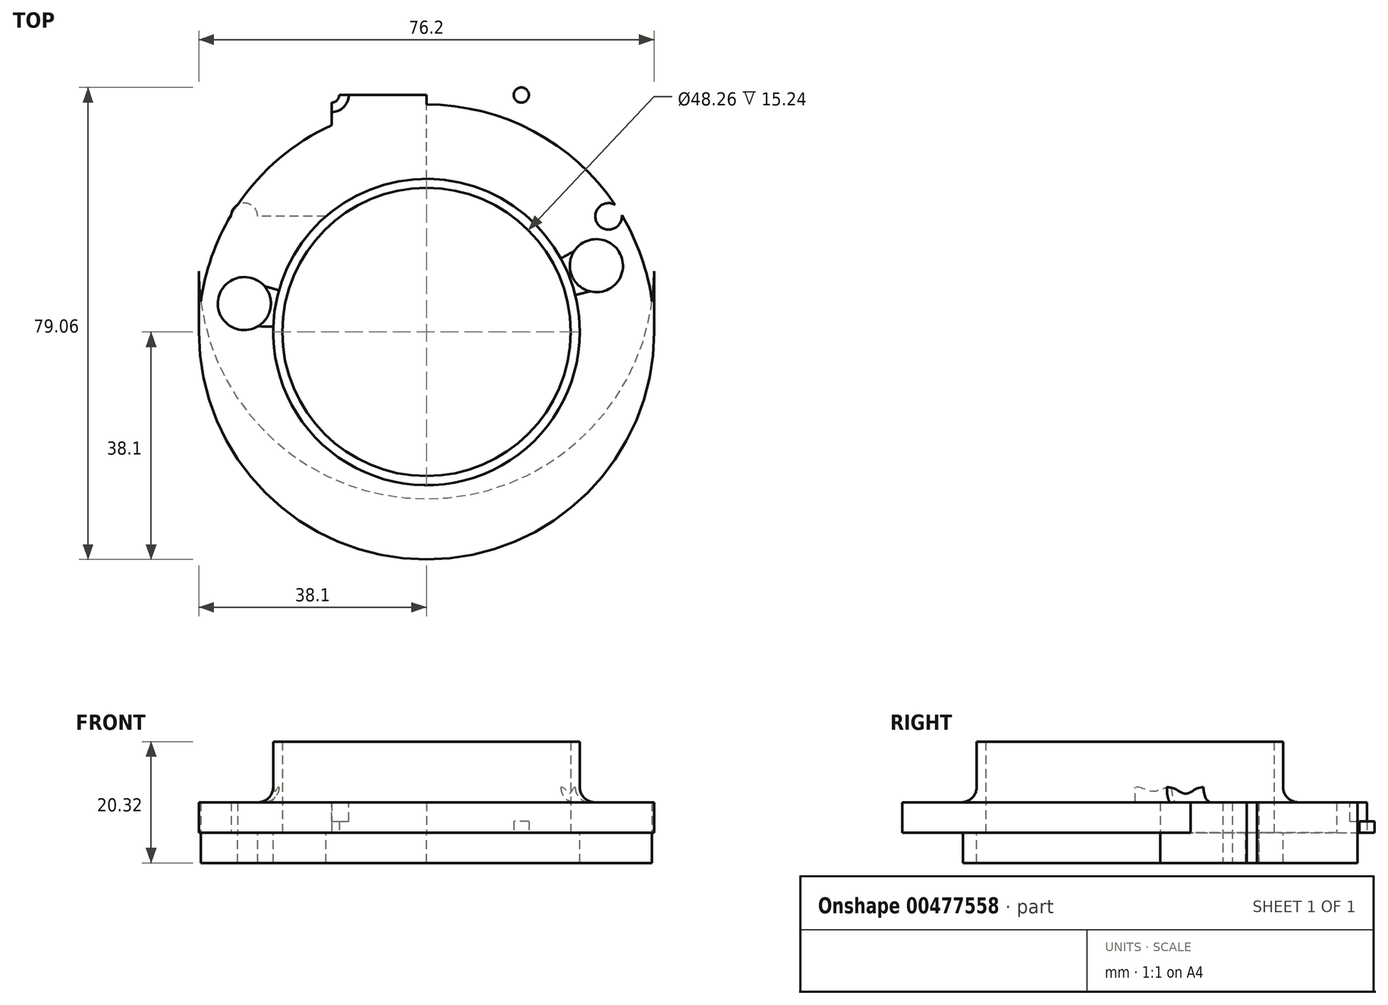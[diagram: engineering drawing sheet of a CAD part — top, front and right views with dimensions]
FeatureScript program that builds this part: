
annotation { "Feature Type Name" : "Feature", "Feature Type Description" : "" }
export const myFeature = defineFeature(function(context is Context, id is Id, definition is map)
    precondition{}
    {
        {
            var Q0;
            Q0=qCreatedBy(makeId("Top.planeOp"),FACE);
            var sketch = newSketch(context, id + "F0", { "sketchPlane" : qUnion([Q0])});
            skLineSegment(sketch, "E0", {"start": v(-15.88, 39.69) * mm, "end": v(15.88, 39.69) * mm});
            skLineSegment(sketch, "E1", {"start": v(0, 0) * mm, "end": v(0, 39.69) * mm});
            skCircle(sketch, "E2", {"center": v(-15.88, 39.69) * mm, "radius": 1.27 * mm});
            skLineSegment(sketch, "E3", {"start": v(-15.88, 19.37) * mm, "end": v(-15.88, 39.69) * mm});
            skCircle(sketch, "E4.MirrorC", {"center": v(15.88, 39.69) * mm, "radius": 1.27 * mm});
            skLineSegment(sketch, "E5", {"start": v(-15.88, 19.37) * mm, "end": v(-30.48, 19.37) * mm});
            skCircle(sketch, "E6", {"center": v(-30.48, 19.37) * mm, "radius": 2.22 * mm});
            skCircle(sketch, "E7.MirrorC", {"center": v(30.48, 19.37) * mm, "radius": 2.22 * mm});
            skCircle(sketch, "E8", {"center": v(0, 0) * mm, "radius": 24.13 * mm});
            skCircle(sketch, "E9", {"center": v(28.45, 11.11) * mm, "radius": 4.45 * mm});
            skCircle(sketch, "E10", {"center": v(-30.48, 4.76) * mm, "radius": 4.45 * mm});
            skCircle(sketch, "E11", {"center": v(0, 0) * mm, "radius": 25.65 * mm});
            skCircle(sketch, "E12", {"center": v(0, 0) * mm, "radius": 38.1 * mm});
            skCircle(sketch, "E13", {"center": v(0, 10.16) * mm, "radius": 38.1 * mm});
            skLineSegment(sketch, "E14", {"start": v(-38.1, 10.16) * mm, "end": v(-38.1, 0) * mm});
            skLineSegment(sketch, "E15", {"start": v(38.1, 10.16) * mm, "end": v(38.1, 0) * mm});
            skSolve(sketch);
        }
        {
            var Q0;
            Q0=makeQuery(id+"F0.imprint","IMPRINT",FACE,{"disambiguationData":[TD([[makeQuery(id+"F0.imprint","IMPRINT",EDGE,{"derivedFrom":sQuery(id+"F0.wireOp",EDGE,"E4.MirrorC")}),1.0]])]});
            var Q1;
            Q1=makeQuery(id+"F0.imprint","IMPRINT",FACE,{"disambiguationData":[TD([[makeQuery(id+"F0.imprint","IMPRINT",EDGE,{"derivedFrom":sQuery(id+"F0.wireOp",EDGE,"E7.MirrorC")}),-1.0]])]});
            var Q2;
            {var subQ1=sQuery(id+"F0.wireOp",EDGE,"E0");var subQ7=sQuery(id+"F0.wireOp",EDGE,"E1");var subQ8=makeQuery(id+"F0.imprint","INTERSECT",VERTEX,{"derivedFrom":[subQ1,subQ7]});Q2=makeQuery(id+"F0.imprint","IMPRINT",FACE,{"disambiguationData":[TD([[makeQuery(id+"F0.imprint","IMPRINT",EDGE,{"disambiguationData":[TD([[subQ8,1.0]])],"derivedFrom":subQ1}),-1.0]])]});}
            var Q3;
            {var subQ0=sQuery(id+"F0.wireOp",EDGE,"E11");var subQ1=sQuery(id+"F0.wireOp",EDGE,"E1");var subQ2=makeQuery(id+"F0.imprint","INTERSECT",VERTEX,{"derivedFrom":[subQ1,subQ0]});Q3=makeQuery(id+"F0.imprint","IMPRINT",FACE,{"disambiguationData":[TD([[makeQuery(id+"F0.imprint","IMPRINT",EDGE,{"disambiguationData":[TD([[subQ2,-1.0]])],"derivedFrom":subQ1}),1.0]])]});}
            var Q4;
            {var subQ5=sQuery(id+"F0.wireOp",EDGE,"E11");var subQ6=sQuery(id+"F0.wireOp",EDGE,"E3");var subQ7=makeQuery(id+"F0.imprint","INTERSECT",VERTEX,{"derivedFrom":[subQ6,subQ5]});Q4=makeQuery(id+"F0.imprint","IMPRINT",FACE,{"disambiguationData":[TD([[makeQuery(id+"F0.imprint","IMPRINT",EDGE,{"disambiguationData":[TD([[subQ7,-1.0]])],"derivedFrom":subQ6}),1.0]])]});}
            var Q5;
            Q5=makeQuery(id+"F0.imprint","IMPRINT",FACE,{"disambiguationData":[TD([[makeQuery(id+"F0.imprint","IMPRINT",EDGE,{"derivedFrom":sQuery(id+"F0.wireOp",EDGE,"E9")}),-1.0]])]});
            var Q6;
            {var subQ0=sQuery(id+"F0.wireOp",EDGE,"E6");var subQ1=makeQuery(id+"F0.imprint","INTERSECT",VERTEX,{"derivedFrom":[sQuery(id+"F0.wireOp",EDGE,"E5"),subQ0]});Q6=makeQuery(id+"F0.imprint","IMPRINT",FACE,{"disambiguationData":[TD([[makeQuery(id+"F0.imprint","IMPRINT",EDGE,{"disambiguationData":[TD([[subQ1,-1.0]])],"derivedFrom":subQ0}),1.0]])]});}
            var Q7;
            {var subQ0=sQuery(id+"F0.wireOp",EDGE,"E12");var subQ1=sQuery(id+"F0.wireOp",EDGE,"E6");var subQ2=makeQuery(id+"F0.imprint","INTERSECT",VERTEX,{"disambiguationData":[OD(0.0)],"derivedFrom":[subQ1,subQ0]});Q7=makeQuery(id+"F0.imprint","IMPRINT",FACE,{"disambiguationData":[TD([[makeQuery(id+"F0.imprint","IMPRINT",EDGE,{"disambiguationData":[TD([[subQ2,-1.0]])],"derivedFrom":subQ1}),1.0]])]});}
            var Q8;
            {var subQ0=sQuery(id+"F0.wireOp",EDGE,"E12");var subQ1=makeQuery(id+"F0.imprint","INTERSECT",VERTEX,{"derivedFrom":[subQ0,sQuery(id+"F0.wireOp",EDGE,"E15")]});Q8=makeQuery(id+"F0.imprint","IMPRINT",FACE,{"disambiguationData":[TD([[makeQuery(id+"F0.imprint","IMPRINT",EDGE,{"disambiguationData":[TD([[subQ1,-1.0]])],"derivedFrom":subQ0}),1.0]])]});}
            var Q9;
            Q9=makeQuery(id+"F0.imprint","IMPRINT",FACE,{"disambiguationData":[TD([[makeQuery(id+"F0.imprint","IMPRINT",EDGE,{"derivedFrom":sQuery(id+"F0.wireOp",EDGE,"E8")}),-1.0]])]});
            var Q10;
            {var subQ0=sQuery(id+"F0.wireOp",EDGE,"E15");Q10=makeQuery(id+"F0.imprint","IMPRINT",FACE,{"disambiguationData":[TD([[makeQuery(id+"F0.imprint","IMPRINT",EDGE,{"derivedFrom":subQ0}),-1.0]])]});}
            var Q11;
            {var subQ0=sQuery(id+"F0.wireOp",EDGE,"E14");Q11=makeQuery(id+"F0.imprint","IMPRINT",FACE,{"disambiguationData":[TD([[makeQuery(id+"F0.imprint","IMPRINT",EDGE,{"derivedFrom":subQ0}),1.0]])]});}
            extrude(context, id + "F1", {"entities" : qUnion([Q0, Q1, Q2, Q3, Q4, Q5, Q6, Q7, Q8, Q9, Q10, Q11]), "depth" : 5.08 * mm});
        }
        {
            var Q0;
            Q0=makeQuery(id+"F0.imprint","IMPRINT",FACE,{"disambiguationData":[TD([[makeQuery(id+"F0.imprint","IMPRINT",EDGE,{"derivedFrom":sQuery(id+"F0.wireOp",EDGE,"E6")}),1.0]])]});
            var Q1;
            Q1=makeQuery(id+"F0.imprint","IMPRINT",FACE,{"disambiguationData":[TD([[makeQuery(id+"F0.imprint","IMPRINT",EDGE,{"derivedFrom":sQuery(id+"F0.wireOp",EDGE,"E7.MirrorC")}),-1.0]])]});
            extrude(context, id + "F2", {"entities" : qUnion([Q0, Q1]), "operationType" : NewBodyOperationType.ADD, "oppositeDirection" : true, "depth" : 5.08 * mm});
        }
        {
            var Q0;
            Q0=makeQuery(id+"F0.imprint","IMPRINT",FACE,{"disambiguationData":[TD([[makeQuery(id+"F0.imprint","IMPRINT",EDGE,{"derivedFrom":sQuery(id+"F0.wireOp",EDGE,"E8")}),-1.0]])]});
            var Q1;
            {var subQ0=sQuery(id+"F0.wireOp",EDGE,"E5");var subQ1=sQuery(id+"F0.wireOp",EDGE,"E3");var subQ2=makeQuery(id+"F0.imprint","INTERSECT",VERTEX,{"derivedFrom":[subQ1,subQ0]});Q1=makeQuery(id+"F0.imprint","IMPRINT",FACE,{"disambiguationData":[TD([[makeQuery(id+"F0.imprint","IMPRINT",EDGE,{"disambiguationData":[TD([[subQ2,-1.0]])],"derivedFrom":subQ1}),1.0]])]});}
            extrude(context, id + "F3", {"entities" : qUnion([Q0, Q1]), "operationType" : NewBodyOperationType.ADD, "depth" : 15.24 * mm});
        }
        {
            var Q0;
            {var subQ0=sQuery(id+"F0.wireOp",EDGE,"E11");Q0=makeQuery(id+"F3.boolean.opBoolean","INTERSECT",EDGE,{"derivedFrom":[makeQuery(id+"F1.opExtrude","CAP_FACE",FACE,{"disambiguationData":[OSD([sQuery(id+"F0.wireOp",EDGE,"E2"),sQuery(id+"F0.wireOp",EDGE,"E3"),sQuery(id+"F0.wireOp",EDGE,"E4.MirrorC"),sQuery(id+"F0.wireOp",EDGE,"E5"),sQuery(id+"F0.wireOp",EDGE,"E8"),sQuery(id+"F0.wireOp",EDGE,"E9"),sQuery(id+"F0.wireOp",EDGE,"E10"),subQ0,sQuery(id+"F0.wireOp",EDGE,"E12"),sQuery(id+"F0.wireOp",EDGE,"E13"),sQuery(id+"F0.wireOp",EDGE,"E14"),sQuery(id+"F0.wireOp",EDGE,"E15")])],"isStart":false}),makeQuery(id+"F3.opExtrude","SWEPT_FACE",FACE,{"disambiguationData":[OSD([subQ0])]})]});}
            fillet(context, id + "F4", {"entities" : qUnion([Q0]), "radius" : 2.54 * mm, "tangentPropagation" : true, "allowEdgeOverflow" : false});
        }
        {
            var Q0;
            Q0=makeQuery(id+"F1.opExtrude","CAP_FACE",FACE,{"disambiguationData":[OSD([sQuery(id+"F0.wireOp",EDGE,"E2"),sQuery(id+"F0.wireOp",EDGE,"E3"),sQuery(id+"F0.wireOp",EDGE,"E4.MirrorC"),sQuery(id+"F0.wireOp",EDGE,"E5"),sQuery(id+"F0.wireOp",EDGE,"E8"),sQuery(id+"F0.wireOp",EDGE,"E9"),sQuery(id+"F0.wireOp",EDGE,"E10"),sQuery(id+"F0.wireOp",EDGE,"E11"),sQuery(id+"F0.wireOp",EDGE,"E12"),sQuery(id+"F0.wireOp",EDGE,"E13"),sQuery(id+"F0.wireOp",EDGE,"E14"),sQuery(id+"F0.wireOp",EDGE,"E15")])],"isStart":false});
            var sketch = newSketch(context, id + "F5", { "sketchPlane" : qUnion([Q0])});
            skCircle(sketch, "E16", {"center": v(-15.88, 39.69) * mm, "radius": 2.86 * mm});
            skCircle(sketch, "E17", {"center": v(15.88, 39.69) * mm, "radius": 2.86 * mm});
            skSolve(sketch);
        }
        {
            var Q0;
            Q0=makeQuery(id+"F5.imprint","IMPRINT",FACE,{"disambiguationData":[TD([[makeQuery(id+"F5.imprint","IMPRINT",EDGE,{"derivedFrom":sQuery(id+"F5.wireOp",EDGE,"E16")}),1.0]])]});
            var Q1;
            Q1=makeQuery(id+"F5.imprint","IMPRINT",FACE,{"disambiguationData":[TD([[makeQuery(id+"F5.imprint","IMPRINT",EDGE,{"derivedFrom":sQuery(id+"F5.wireOp",EDGE,"E17")}),1.0]])]});
            extrude(context, id + "F6", {"entities" : qUnion([Q0, Q1]), "operationType" : NewBodyOperationType.REMOVE, "oppositeDirection" : true, "depth" : 3.17 * mm});
        }
    });
